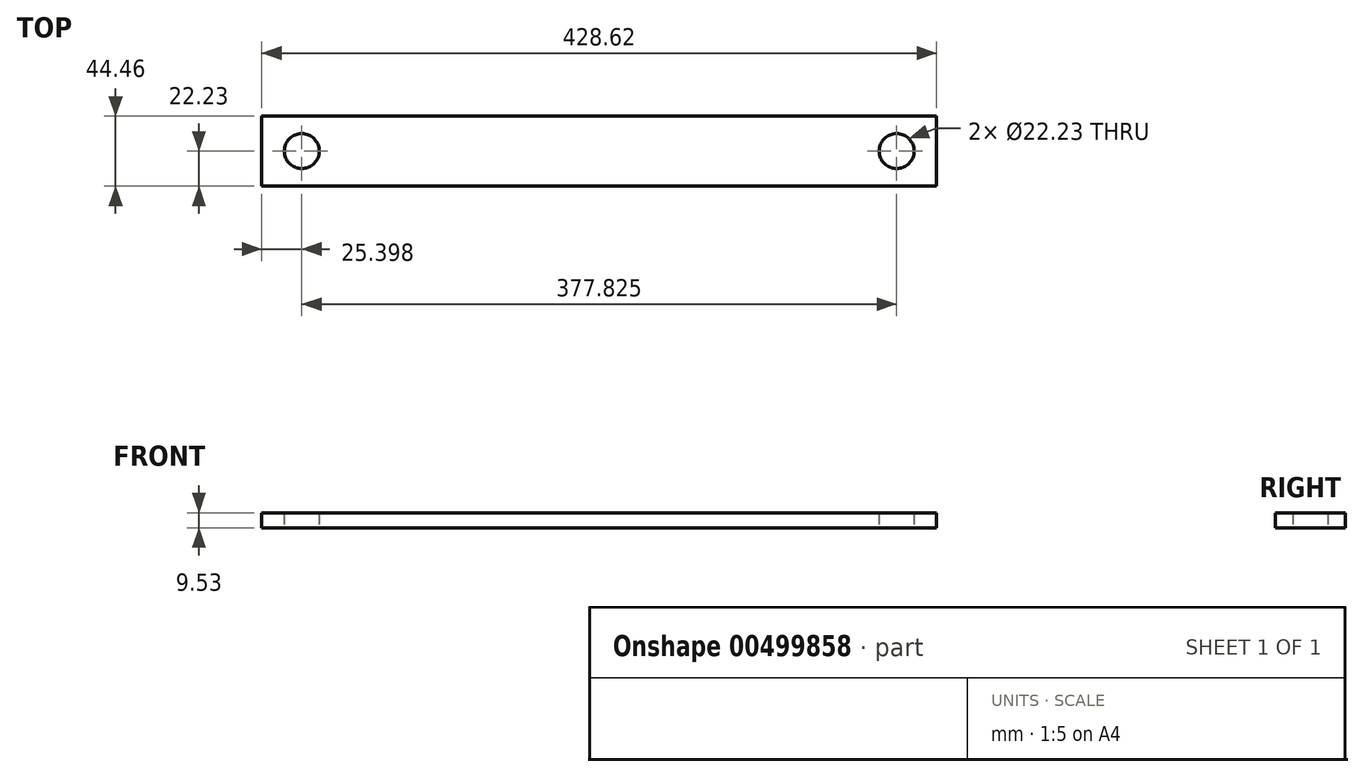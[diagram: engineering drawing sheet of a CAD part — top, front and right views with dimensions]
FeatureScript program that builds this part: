
annotation { "Feature Type Name" : "Feature", "Feature Type Description" : "" }
export const myFeature = defineFeature(function(context is Context, id is Id, definition is map)
    precondition{}
    {
        {
            var Q0;
            Q0=qCreatedBy(makeId("Top.planeOp"),FACE);
            var sketch = newSketch(context, id + "F0", { "sketchPlane" : qUnion([Q0])});
            skLineSegment(sketch, "E0.bottom", {"start": v(214.31, -22.22) * mm, "end": v(-214.31, -22.23) * mm});
            skLineSegment(sketch, "E0.top", {"start": v(214.31, 22.23) * mm, "end": v(-214.31, 22.22) * mm});
            skLineSegment(sketch, "E0.left", {"start": v(214.31, -22.22) * mm, "end": v(214.31, 22.23) * mm});
            skLineSegment(sketch, "E0.right", {"start": v(-214.31, -22.23) * mm, "end": v(-214.31, 22.22) * mm});
            skPoint(sketch, "E0.middle", {"position": v(0, 0) * mm});
            skCircle(sketch, "E1", {"center": v(-188.91, 0) * mm, "radius": 11.11 * mm});
            skCircle(sketch, "E2.MirrorC", {"center": v(188.91, 0) * mm, "radius": 11.11 * mm});
            skSolve(sketch);
        }
        {
            var Q0;
            Q0 = qSketchRegion(id + "F0", true);
            extrude(context, id + "F1", {"entities" : qUnion([Q0]), "depth" : 9.52 * mm});
        }
    });
